# Revit family: IS_ConnectSpace_E1191_BIM_FR
name_source: partatom
category: Plumbing Fixtures
revit_build: Autodesk Revit MEP 2016 (Build: 20161004_0715(x64)
units: mm (PartAtom-declared; Revit-internal decimal feet)

## family parameters
Always vertical = No
Cut with Voids When Loaded = No
OmniClass Number = 23.45.05.21.11.11
OmniClass Title = Water Operated Water Closets
Part Type = Normal
Room Calculation Point = No
Round Connector Dimension = Use Diameter
Shared = No
Work Plane-Based = No

## types (1)
- E1191 - CONNECT SPACE RESERVOIR D'ANGLE BLC
    Accessoires = www.idealspec.fr
    Assembly Code = C1030200
    Auteur = Ideal Standard (Fr)
    BIMobject category = Toilet Cisterns
    BOSUseNativeGeometries = 1
    Brand url = http://www.idealstandard.co.uk
    Caracteristiques = CONNECT SPACE RESERVOIR D'ANGLE BLC
    CodeBarre = 5017830446552
    Couleur = blanc
    CouleurWc = blanc
    CoutDeRemplacement = 0
    DateDeCreation = 26.07.2017
    DebitL/Mn = Litres
    Description = CONNECT SPACE RESERVOIR D'ANGLE BLC
    DetailGarantie = Manufacturers Warranty
    Dimensions = 383 x 300 x 311
    DureeDeGarantieDesPieces = 2
    DureeGarantie = year
    EAN code = https://5017830446552
    Edition number = 1
    Espace = Internal
    Finition = blanc
    Forme = Sculptured
    Hauteur = 383 mm
    IFC Classification = Sanitary Terminal
    IfcExportAs = IfcSanitaryTerminalType
    IfcExportType = CISTERN
    InformationsProduit = http://www.idealspec.fr
    Installation instructions = http://www.idealspec.fr
    Largeur = 300 mm
    LienUtile = www.idealspec.fr
    Longueur = 311 mm
    Manufacturer name = Ideal Standard
    Marque = Ideal Standard
    Material main = Ceramics
    Materiel = vitrifie
    MaterielWc = Vitreous china
    Model = E1191
    NBS Reference Code = 35-93-90
    NBS Reference Description = Wc Cisterns
    Nom = CONNECT SPACE RESERVOIR D'ANGLE BLC
    Nominal height = 775
    Nominal width = 365
    OmniClass Code = 23-31 19 00
    OmniClass Description = Toilets
    PoidsBrut = 12.541
    PoidsNet = 11.76
    Product Guid = f35142df-859c-461b-b538-42367b763718
    Product SKU = E1191
    Product certification = http://www.idealstandard.it
    Product data url = https://bimobject.com
    Product family = CONNECT SPACE
    Product group = Tank
    Product name = CONNECT SPACE TANK WHITE 6/4L DFV
    Product url = http://www.idealstandard.it
    QR code = http://bimobject.com
    Raccordement = Plomberie
    Revision = 1
    Technical description = http://www.idealstandard.it
    Telephone = 0033149382800
    TypeDImmobilisation = Fixed
    Uniclass 1.4 Code = L72164
    Uniclass 1.4 Description = WC cisterns
    Uniclass 2.0 Code = PR-35-93-90
    Uniclass 2.0 Description = Wc Cisterns
    Uniclass 2015 Code = Pr_40_20_93_89
    Uniclass 2015 Name = WC cisterns
    UniteDeMesure = millimeters
    UniteDeTemps = year
    UrlDuFabricant = www.idealspec.fr
    Version = 1
    Weight Net (Kg) = 11.76
    Youtube clip = http://www.idealstandard.it

## geometry (parser evidence)
native form markers: Blend x4, Sweep x1
no freeform markers — native parametric forms only
